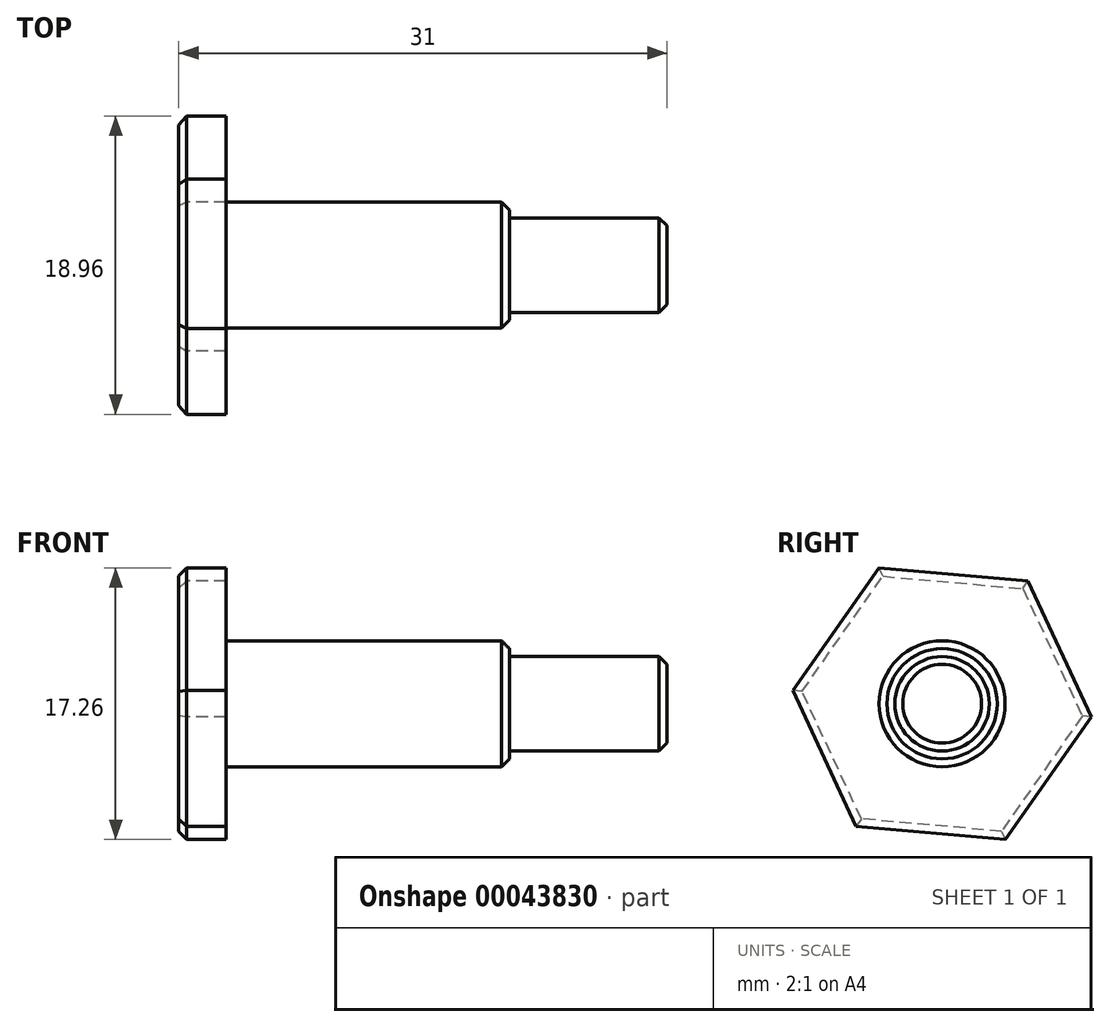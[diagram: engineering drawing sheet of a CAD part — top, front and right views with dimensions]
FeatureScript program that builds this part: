
annotation { "Feature Type Name" : "Feature", "Feature Type Description" : "" }
export const myFeature = defineFeature(function(context is Context, id is Id, definition is map)
    precondition{}
    {
        {
            var Q0;
            Q0=qCreatedBy(makeId("Front.planeOp"),FACE);
            var sketch = newSketch(context, id + "F0", { "sketchPlane" : qUnion([Q0])});
            skLineSegment(sketch, "E0", {"start": v(0, 0) * mm, "end": v(31, 0) * mm});
            skLineSegment(sketch, "E1", {"start": v(0, 0) * mm, "end": v(0, 10) * mm});
            skLineSegment(sketch, "E2.0", {"start": v(3, 4) * mm, "end": v(3, 10) * mm});
            skLineSegment(sketch, "E3.0", {"start": v(21, 3) * mm, "end": v(21, 4) * mm});
            skLineSegment(sketch, "E4.0", {"start": v(31, 0) * mm, "end": v(31, 3) * mm});
            skLineSegment(sketch, "E5.trimOffspring", {"start": v(21, 3) * mm, "end": v(31, 3) * mm});
            skLineSegment(sketch, "E6.0", {"start": v(3, 4) * mm, "end": v(21, 4) * mm});
            skLineSegment(sketch, "E7.0", {"start": v(0, 10) * mm, "end": v(3, 10) * mm});
            skSolve(sketch);
        }
        {
            var Q0;
            Q0 = qSketchRegion(id + "F0", true);
            var Q1;
            Q1=sQuery(id+"F0.wireOp",EDGE,"E0");
            revolve(context, id + "F1", {"entities" : qUnion([Q0]), "axis" : qUnion([Q1]), "revolveType" : RevolveType.FULL});
        }
        {
            var Q0;
            Q0=makeQuery(id+"F1.opRevolve","SWEPT_FACE",FACE,{"disambiguationData":[OSD([sQuery(id+"F0.wireOp",EDGE,"E1")])]});
            var sketch = newSketch(context, id + "F2", { "sketchPlane" : qUnion([Q0])});
            skCircle(sketch, "E8.cCircle", {"center": v(0, 0) * mm, "radius": 8.24 * mm, "construction": true});
            skLineSegment(sketch, "E8.0", {"start": v(4.01, 8.63) * mm, "end": v(9.48, 0.84) * mm});
            skLineSegment(sketch, "E8.1", {"start": v(9.48, 0.84) * mm, "end": v(5.46, -7.79) * mm});
            skLineSegment(sketch, "E8.2", {"start": v(5.46, -7.79) * mm, "end": v(-4.01, -8.63) * mm});
            skLineSegment(sketch, "E8.3", {"start": v(-4.01, -8.63) * mm, "end": v(-9.48, -0.84) * mm});
            skLineSegment(sketch, "E8.4", {"start": v(-9.48, -0.84) * mm, "end": v(-5.46, 7.79) * mm});
            skLineSegment(sketch, "E8.5", {"start": v(-5.46, 7.79) * mm, "end": v(4.01, 8.63) * mm});
            skPoint(sketch, "E8.0.midPoint", {"position": v(6.74, 4.73) * mm});
            skCircle(sketch, "E9", {"center": v(0, 0) * mm, "radius": 11.38 * mm});
            skSolve(sketch);
        }
        {
            var Q0;
            Q0 = qSketchRegion(id + "F2", true);
            extrude(context, id + "F3", {"entities" : qUnion([Q0]), "operationType" : NewBodyOperationType.REMOVE, "oppositeDirection" : true, "depth" : 25 * mm});
        }
        {
            var Q0;
            Q0=makeQuery(id+"F1.opRevolve","SWEPT_EDGE",EDGE,{"disambiguationData":[OSD([sQuery(id+"F0.wireOp",EDGE,"E3.0"),sQuery(id+"F0.wireOp",EDGE,"E6.0")])]});
            chamfer(context, id + "F4", {"entities" : qUnion([Q0]), "width" : 0.5 * mm, "tangentPropagation" : true});
        }
        {
            var Q0;
            Q0=makeQuery(id+"F1.opRevolve","SWEPT_EDGE",EDGE,{"disambiguationData":[OSD([sQuery(id+"F0.wireOp",EDGE,"E4.0"),sQuery(id+"F0.wireOp",EDGE,"E5.trimOffspring")])]});
            chamfer(context, id + "F5", {"entities" : qUnion([Q0]), "width" : 0.5 * mm, "tangentPropagation" : true});
        }
        {
            var Q0;
            Q0=makeQuery(id+"F1.opRevolve","SWEPT_FACE",FACE,{"disambiguationData":[OSD([sQuery(id+"F0.wireOp",EDGE,"E1")])]});
            chamfer(context, id + "F6", {"entities" : qUnion([Q0]), "width" : 0.5 * mm, "tangentPropagation" : true});
        }
    });
